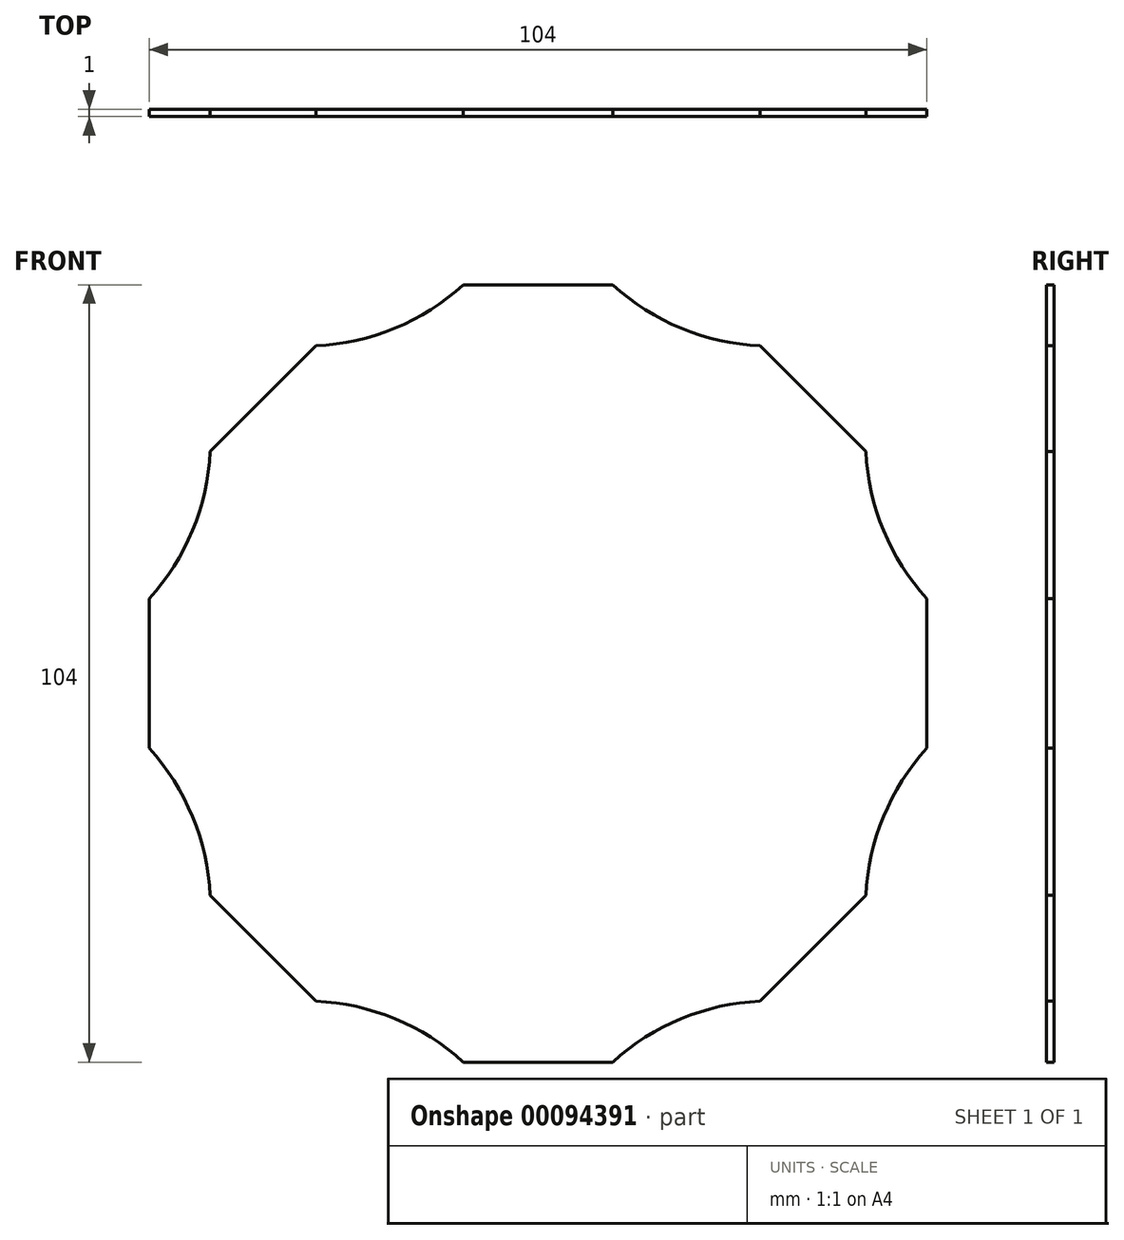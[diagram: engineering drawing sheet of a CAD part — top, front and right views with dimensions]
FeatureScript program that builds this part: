
annotation { "Feature Type Name" : "Feature", "Feature Type Description" : "" }
export const myFeature = defineFeature(function(context is Context, id is Id, definition is map)
    precondition{}
    {
        {
            var Q0;
            Q0=qCreatedBy(makeId("Front.planeOp"),FACE);
            var sketch = newSketch(context, id + "F0", { "sketchPlane" : qUnion([Q0])});
            skCircle(sketch, "E0", {"center": v(0, 0) * mm, "radius": 50 * mm, "construction": true});
            skLineSegment(sketch, "E1", {"start": v(-10, 52) * mm, "end": v(10, 52) * mm});
            skLineSegment(sketch, "E2", {"start": v(0, 0) * mm, "end": v(0, 52) * mm, "construction": true});
            skLineSegment(sketch, "E3", {"start": v(-36.77, 36.77) * mm, "end": v(0, 0) * mm, "construction": true});
            skLineSegment(sketch, "E4", {"start": v(0, 0) * mm, "end": v(-52, 0) * mm, "construction": true});
            skLineSegment(sketch, "E5", {"start": v(-43.84, 29.7) * mm, "end": v(-29.7, 43.84) * mm});
            skLineSegment(sketch, "E6", {"start": v(-52, 10) * mm, "end": v(-52, -10) * mm});
            skArc(sketch, "E7", {"start": v(-29.7, 43.84) * mm, "mid": v(-19.13, 46.2) * mm, "end": v(-10, 52) * mm});
            skArc(sketch, "E8.MirrorCS", {"start": v(-43.84, 29.7) * mm, "mid": v(-46.2, 19.13) * mm, "end": v(-52, 10) * mm});
            skArc(sketch, "E9.MirrorCS", {"start": v(29.7, 43.84) * mm, "mid": v(19.13, 46.2) * mm, "end": v(10, 52) * mm});
            skLineSegment(sketch, "E10.MirrorCS", {"start": v(43.84, 29.7) * mm, "end": v(29.7, 43.84) * mm});
            skArc(sketch, "E11.MirrorCS", {"start": v(43.84, 29.7) * mm, "mid": v(46.2, 19.13) * mm, "end": v(52, 10) * mm});
            skLineSegment(sketch, "E12.MirrorCS", {"start": v(52, 10) * mm, "end": v(52, -10) * mm});
            skArc(sketch, "E13.MirrorCS", {"start": v(-43.84, -29.7) * mm, "mid": v(-46.2, -19.13) * mm, "end": v(-52, -10) * mm});
            skLineSegment(sketch, "E14.MirrorCS", {"start": v(-43.84, -29.7) * mm, "end": v(-29.7, -43.84) * mm});
            skArc(sketch, "E15.MirrorCS", {"start": v(-29.7, -43.84) * mm, "mid": v(-19.13, -46.2) * mm, "end": v(-10, -52) * mm});
            skLineSegment(sketch, "E16.MirrorCS", {"start": v(-10, -52) * mm, "end": v(10, -52) * mm});
            skArc(sketch, "E17.MirrorCS", {"start": v(29.7, -43.84) * mm, "mid": v(19.13, -46.2) * mm, "end": v(10, -52) * mm});
            skLineSegment(sketch, "E18.MirrorCS", {"start": v(43.84, -29.7) * mm, "end": v(29.7, -43.84) * mm});
            skArc(sketch, "E19.MirrorCS", {"start": v(43.84, -29.7) * mm, "mid": v(46.2, -19.13) * mm, "end": v(52, -10) * mm});
            skSolve(sketch);
        }
        {
            var Q0;
            Q0 = qSketchRegion(id + "F0", true);
            extrude(context, id + "F1", {"entities" : qUnion([Q0]), "depth" : 1 * mm});
        }
    });
